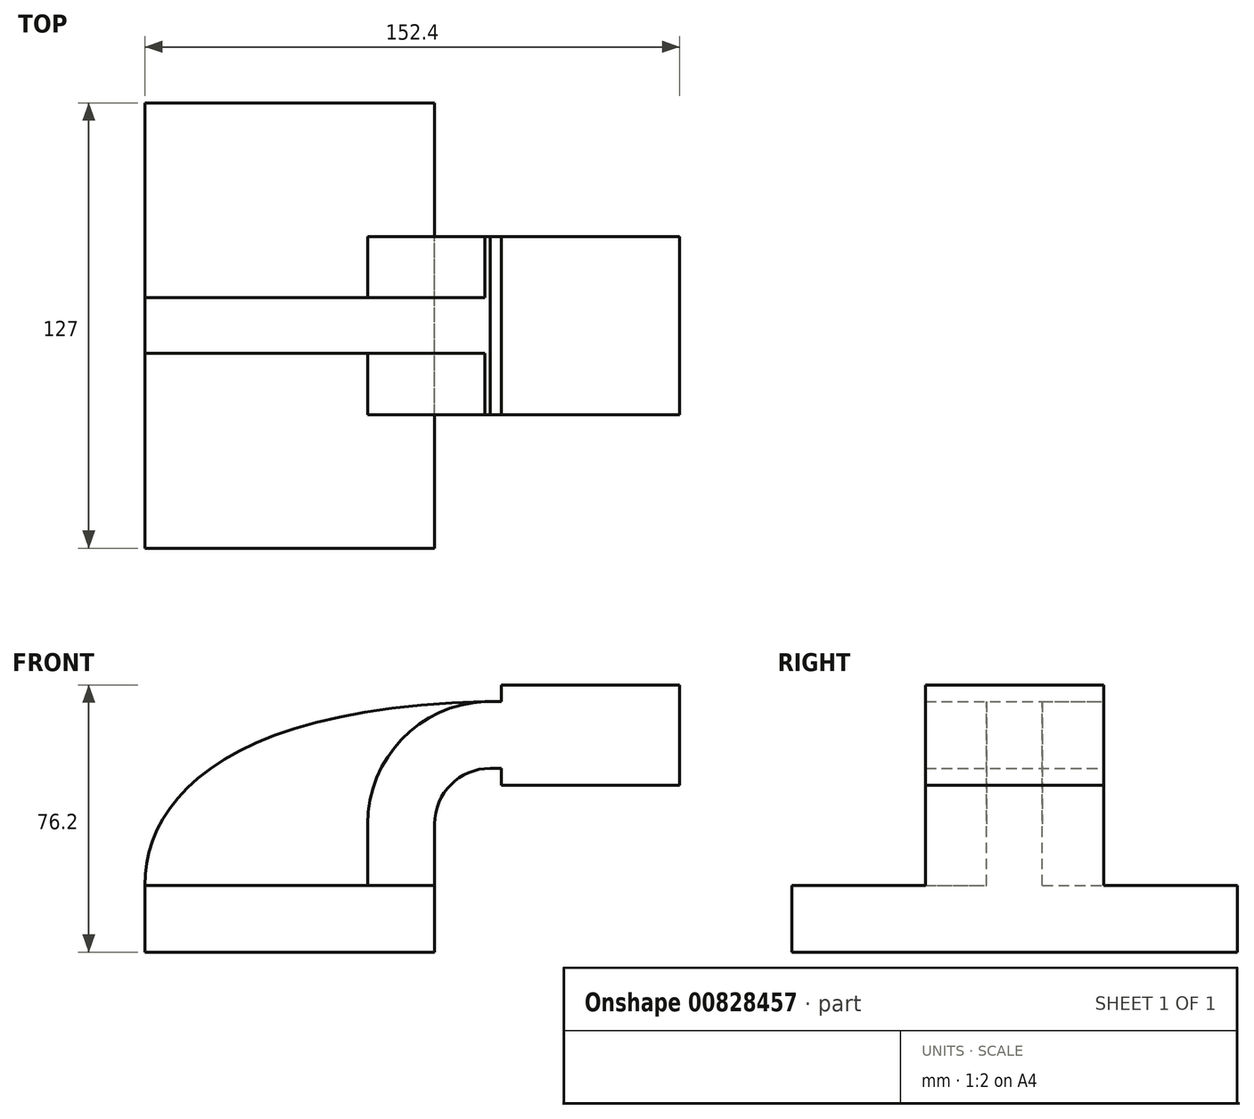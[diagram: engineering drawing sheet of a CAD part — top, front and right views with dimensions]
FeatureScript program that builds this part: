
annotation { "Feature Type Name" : "Feature", "Feature Type Description" : "" }
export const myFeature = defineFeature(function(context is Context, id is Id, definition is map)
    precondition{}
    {
        {
            var Q0;
            Q0=qCreatedBy(makeId("Front.planeOp"),FACE);
            var sketch = newSketch(context, id + "F0", { "sketchPlane" : qUnion([Q0])});
            skLineSegment(sketch, "E0.bottom", {"start": v(-41.28, 9.52) * mm, "end": v(41.28, 9.53) * mm});
            skLineSegment(sketch, "E0.top", {"start": v(-41.28, -9.53) * mm, "end": v(41.28, -9.53) * mm});
            skLineSegment(sketch, "E0.left", {"start": v(-41.28, 9.52) * mm, "end": v(-41.28, -9.53) * mm});
            skLineSegment(sketch, "E0.right", {"start": v(41.28, 9.53) * mm, "end": v(41.28, -9.52) * mm});
            skPoint(sketch, "E0.middle", {"position": v(0, 0) * mm});
            skLineSegment(sketch, "E1.bottom", {"start": v(60.32, 66.68) * mm, "end": v(111.12, 66.68) * mm});
            skLineSegment(sketch, "E1.top", {"start": v(60.32, 38.1) * mm, "end": v(111.12, 38.1) * mm});
            skLineSegment(sketch, "E1.left", {"start": v(60.32, 66.68) * mm, "end": v(60.32, 38.1) * mm});
            skLineSegment(sketch, "E1.right", {"start": v(111.12, 66.68) * mm, "end": v(111.12, 38.1) * mm});
            skPoint(sketch, "E1.middle", {"position": v(85.72, 52.39) * mm});
            skLineSegment(sketch, "E2", {"start": v(41.27, 9.53) * mm, "end": v(41.27, 27) * mm});
            skArc(sketch, "E3", {"start": v(41.27, 27) * mm, "mid": v(45.92, 38.23) * mm, "end": v(57.15, 42.88) * mm});
            skLineSegment(sketch, "E4", {"start": v(57.15, 42.88) * mm, "end": v(95.35, 42.88) * mm});
            skLineSegment(sketch, "E5.0", {"start": v(57.15, 61.93) * mm, "end": v(95.35, 61.93) * mm});
            skArc(sketch, "E5.1", {"start": v(22.22, 27) * mm, "mid": v(32.45, 51.7) * mm, "end": v(57.15, 61.93) * mm});
            skLineSegment(sketch, "E5.2", {"start": v(22.23, 9.53) * mm, "end": v(22.23, 27) * mm});
            skFitSpline(sketch, "E6", {"points": [v(-41.28, 9.53) * mm, v(57.15, 61.93) * mm], "startDerivative": vector(-0.22, 72.94) * mm, "endDerivative": vector(226.74, 4.35) * mm});
            skSolve(sketch);
        }
        {
            var Q0;
            Q0=makeQuery(id+"F0.imprint","IMPRINT",FACE,{"disambiguationData":[TD([[makeQuery(id+"F0.imprint","IMPRINT",EDGE,{"derivedFrom":sQuery(id+"F0.wireOp",EDGE,"E0.top")}),1.0]])]});
            extrude(context, id + "F1", {"entities" : qUnion([Q0]), "endBound" : BoundingType.SYMMETRIC, "depth" : 127 * mm, "offsetDistance" : 25.4 * mm});
        }
        {
            var Q0;
            {var subQ3=sQuery(id+"F0.wireOp",EDGE,"E1.bottom");Q0=makeQuery(id+"F0.imprint","IMPRINT",FACE,{"disambiguationData":[TD([[makeQuery(id+"F0.imprint","IMPRINT",EDGE,{"derivedFrom":subQ3}),-1.0]])]});}
            var Q1;
            {var subQ1=sQuery(id+"F0.wireOp",EDGE,"E2");Q1=makeQuery(id+"F0.imprint","IMPRINT",FACE,{"disambiguationData":[TD([[makeQuery(id+"F0.imprint","IMPRINT",EDGE,{"derivedFrom":subQ1}),1.0]])]});}
            extrude(context, id + "F2", {"entities" : qUnion([Q0, Q1]), "operationType" : NewBodyOperationType.ADD, "endBound" : BoundingType.SYMMETRIC, "depth" : 50.8 * mm, "offsetDistance" : 25.4 * mm});
        }
        {
            var Q0;
            {var subQ3=sQuery(id+"F0.wireOp",EDGE,"E5.2");Q0=makeQuery(id+"F0.imprint","IMPRINT",FACE,{"disambiguationData":[TD([[makeQuery(id+"F0.imprint","IMPRINT",EDGE,{"derivedFrom":subQ3}),1.0]])]});}
            extrude(context, id + "F3", {"entities" : qUnion([Q0]), "operationType" : NewBodyOperationType.ADD, "endBound" : BoundingType.SYMMETRIC, "depth" : 15.88 * mm, "offsetDistance" : 25.4 * mm});
        }
    });
